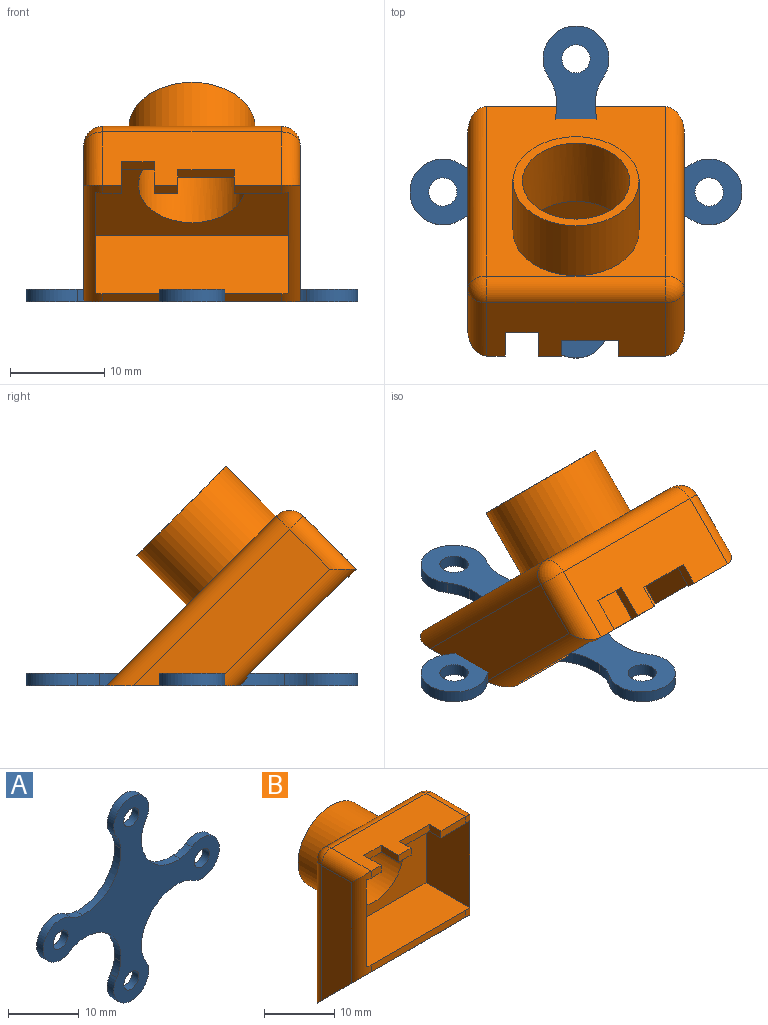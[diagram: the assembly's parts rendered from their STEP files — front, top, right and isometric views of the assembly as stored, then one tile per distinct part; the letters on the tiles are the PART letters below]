
ASSEMBLY  parts=2 mates=1
PART A: 22 faces, bbox 35.3x1.3x35.3 mm
  f0: cylinder r=5mm len=2.39mm, axis (0,1,0), area 3.3mm2, adj f1,f19,f20,f21
  f1: cylinder r=3.5mm len=7mm, axis (0,1,0), area 19.7mm2, adj f0,f2,f20,f21
  f2: cylinder r=5mm len=2.39mm, axis (0,1,0), area 3.3mm2, adj f1,f3,f20,f21
  f3: cylinder r=7.18mm len=7.75mm, axis (0,1,0), area 16.1mm2, adj f2,f4,f20,f21
  f4: cylinder r=5mm len=2.39mm, axis (0,1,0), area 3.3mm2, adj f3,f5,f20,f21
  f5: cylinder r=3.5mm len=7mm, axis (0,1,0), area 19.7mm2, adj f4,f6,f20,f21
  f6: cylinder r=5mm len=2.39mm, axis (0,1,0), area 3.3mm2, adj f5,f7,f20,f21
  f7: cylinder r=7.18mm len=7.75mm, axis (0,1,0), area 16.1mm2, adj f6,f8,f20,f21
  f8: cylinder r=5mm len=2.39mm, axis (0,1,0), area 3.3mm2, adj f7,f9,f20,f21
  f9: cylinder r=3.5mm len=7mm, axis (0,1,0), area 19.7mm2, adj f8,f10,f20,f21
  f10: cylinder r=5mm len=2.39mm, axis (0,1,0), area 3.3mm2, adj f9,f11,f20,f21
  f11: cylinder r=7.18mm len=7.75mm, axis (0,1,0), area 16.1mm2, adj f10,f12,f20,f21
  f12: cylinder r=5mm len=2.39mm, axis (0,1,0), area 3.3mm2, adj f11,f13,f20,f21
  f13: cylinder r=3.5mm len=7mm, axis (0,1,0), area 19.7mm2, adj f12,f14,f20,f21
  f14: cylinder r=5mm len=2.39mm, axis (0,1,0), area 3.3mm2, adj f13,f19,f20,f21
  f15: cylinder r=1.5mm len=3mm, axis (0,1,0), area 12.3mm2, adj f20,f21
  f16: cylinder r=1.5mm len=3mm, axis (0,1,0), area 12.3mm2, adj f20,f21
  f17: cylinder r=1.5mm len=3mm, axis (0,1,0), area 12.3mm2, adj f20,f21
  f18: cylinder r=1.5mm len=3mm, axis (0,1,0), area 12.3mm2, adj f20,f21
  f19: cylinder r=7.18mm len=7.75mm, axis (0,1,0), area 16.1mm2, adj f0,f14,f20,f21
  f20: plane 35.28x35.28mm, normal (0,-1,0), area 333.8mm2, adj f0,f1,f2,f3,f4,f5,f6,f7
  f21: plane 35.28x35.28mm, normal (0,1,0), area 333.8mm2, adj f0,f1,f2,f3,f4,f5,f6,f7
PART B: 32 faces, bbox 23x17.5x27.5 mm
  f0: plane 19x1.2mm, normal (0,-1,0), area 22.8mm2, adj f9,f22,f23,f29
  f1: plane 2x1.2mm, normal (0,-1,0), area 2.4mm2, adj f5,f6,f16,f23
  f2: plane 5x1.2mm, normal (0,-1,0), area 6mm2, adj f5,f6,f19,f29
  f3: plane 23.5x6mm, normal (1,0,0), area 123mm2, adj f22,f28,f29,f31
  f4: plane 2.5x1.2mm, normal (0,-1,0), area 3mm2, adj f5,f6,f17,f21
  f5: plane 19x8mm, normal (0,0,1), area 126mm2, adj f1,f2,f4,f16,f17,f18,f19,f20
  f6: plane 20.6x8.8mm, normal (0,0,-1), area 155.1mm2, adj f1,f2,f4,f10,f11,f12,f16,f17
  f7: plane 23.5x6mm, normal (-1,0,0), area 123mm2, adj f22,f23,f24,f25
  f8: plane 25.5x19mm, normal (0,1,0), area 343.5mm2, adj f14,f22,f25,f27,f28
  f9: plane 20.6x8.8mm, normal (0,0,1), area 181.2mm2, adj f0,f10,f11,f12,f23,f29
  f10: plane 15.1x8.63mm, normal (-1,0,0), area 130.4mm2, adj f6,f9,f12,f29
  f11: plane 15.1x8.63mm, normal (1,0,0), area 130.4mm2, adj f6,f9,f12,f23
  f12: plane 20.6x15.1mm, normal (0,-1,0), area 209mm2, adj f6,f9,f10,f11,f13
  f13: cylinder r=5.7mm len=11.4mm, axis (0,1,0), area 311.6mm2, adj f12,f15
  f14: cylinder r=6.7mm len=13.4mm, axis (0,-1,0), area 315.7mm2, adj f8,f15
  f15: plane 13.4x13.4mm, normal (0,1,0), area 39mm2, adj f13,f14
  f16: plane 3.5x1.2mm, normal (1,0,0), area 4.2mm2, adj f1,f5,f6,f18
  f17: plane 3.5x1.2mm, normal (-1,0,0), area 4.2mm2, adj f4,f5,f6,f18
  f18: plane 3.5x1.2mm, normal (0,-1,0), area 4.2mm2, adj f5,f6,f16,f17
  f19: plane 2.3x1.2mm, normal (-1,0,0), area 2.8mm2, adj f2,f5,f6,f20
  f20: plane 6x1.2mm, normal (0,-1,0), area 7.2mm2, adj f5,f6,f19,f21
  f21: plane 2.3x1.2mm, normal (1,0,0), area 2.8mm2, adj f4,f5,f6,f20
  f22: plane 23x10mm, normal (0,-0.71,-0.71), area 320.4mm2, adj f0,f3,f7,f8,f23,f25,f28,f29
  f23: cylinder r=2mm len=19.5mm, axis (0,0,1), area 42.6mm2, adj f0,f1,f6,f7,f9,f11,f22,f24
  f24: cylinder r=2mm len=8mm, axis (0,-1,0), area 22.8mm2, adj f5,f7,f23,f26
  f25: cylinder r=2mm len=25.5mm, axis (0,0,-1), area 77.8mm2, adj f7,f8,f22,f26
  f26: sphere r=2mm, area 6.3mm2, adj f24,f25,f27
  f27: cylinder r=2mm len=19mm, axis (-1,0,0), area 59.7mm2, adj f5,f8,f26,f30
  f28: cylinder r=2mm len=25.5mm, axis (0,0,1), area 77.8mm2, adj f3,f8,f22,f30
  f29: cylinder r=2mm len=19.5mm, axis (0,0,-1), area 42.6mm2, adj f0,f2,f3,f6,f9,f10,f22,f31
  f30: sphere r=2mm, area 6.3mm2, adj f27,f28,f31
  f31: cylinder r=2mm len=8mm, axis (0,1,0), area 22.8mm2, adj f3,f5,f29,f30
PLACE A rot(axis=(1,0,0),90deg) t=(-2.53,-1.43,2.02)mm
PLACE B rot(axis=(1,0,0),45deg) t=(-2.53,-5.62,13.97)mm
MATE fastened B.f22 <-> A.f20  axis (0,0,-1) through (-2.53,0.57,0.72)mm
